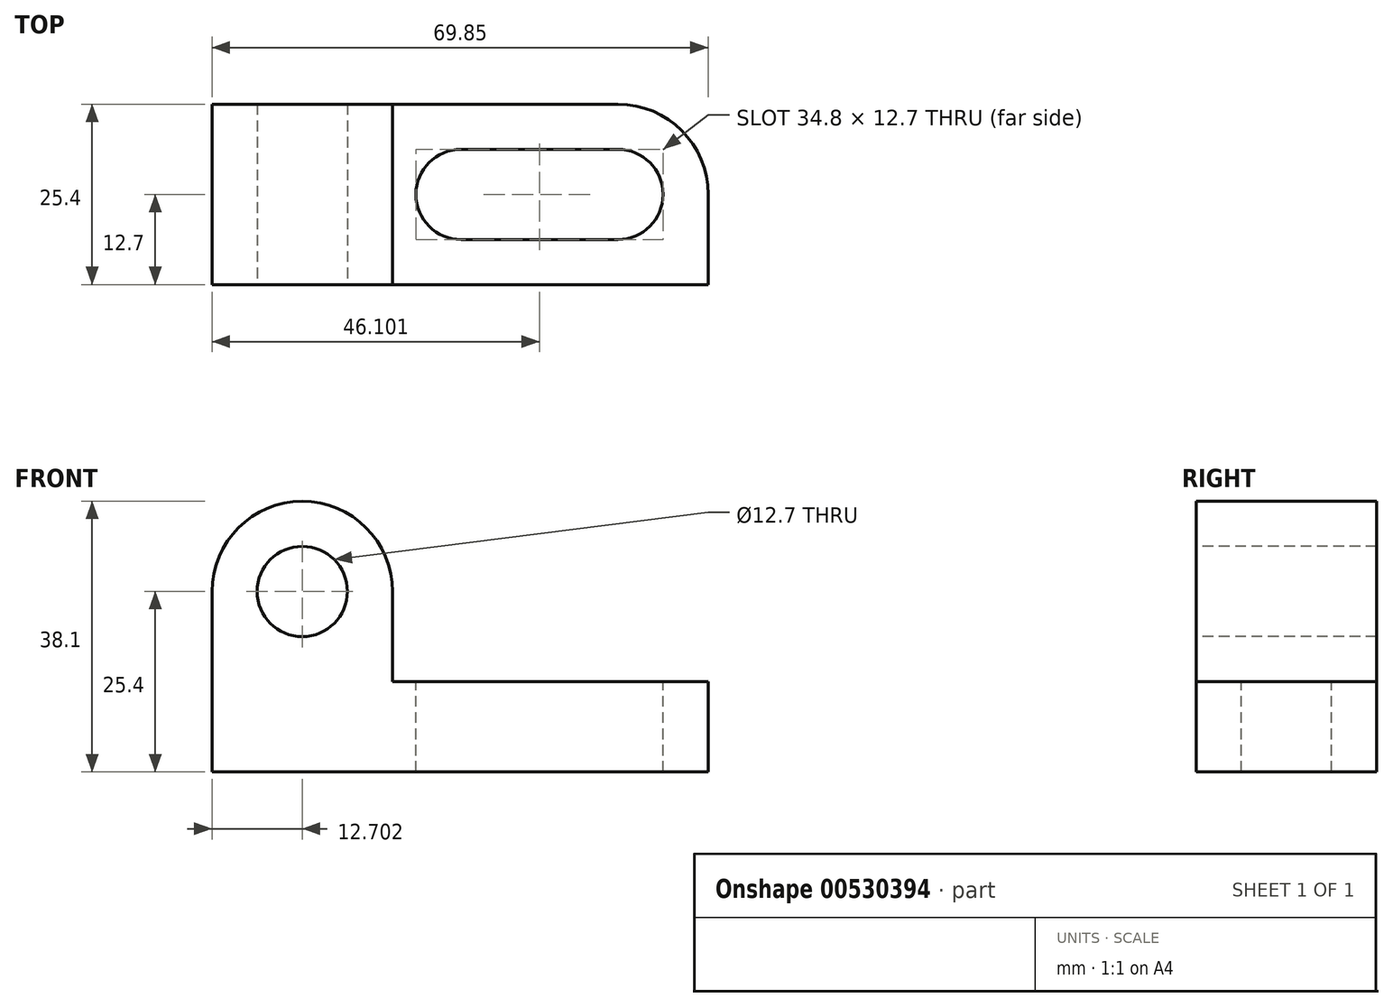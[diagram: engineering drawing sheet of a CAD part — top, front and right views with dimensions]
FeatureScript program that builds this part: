
annotation { "Feature Type Name" : "Feature", "Feature Type Description" : "" }
export const myFeature = defineFeature(function(context is Context, id is Id, definition is map)
    precondition{}
    {
        {
            var Q0;
            Q0=qCreatedBy(makeId("Front.planeOp"),FACE);
            var sketch = newSketch(context, id + "F0", { "sketchPlane" : qUnion([Q0])});
            skLineSegment(sketch, "E0", {"start": v(-35.05, 38.1) * mm, "end": v(-35.05, 0) * mm});
            skLineSegment(sketch, "E1", {"start": v(-35.05, 0) * mm, "end": v(34.8, 0) * mm});
            skLineSegment(sketch, "E2", {"start": v(34.8, 0) * mm, "end": v(34.8, 38.1) * mm});
            skLineSegment(sketch, "E3", {"start": v(34.8, 38.1) * mm, "end": v(-35.05, 38.1) * mm});
            skSolve(sketch);
        }
        {
            var Q0;
            Q0=makeQuery(id+"F0.imprint","IMPRINT",FACE,{"disambiguationData":[TD([[makeQuery(id+"F0.imprint","IMPRINT",EDGE,{"derivedFrom":sQuery(id+"F0.wireOp",EDGE,"E0")}),1.0]])]});
            extrude(context, id + "F1", {"entities" : qUnion([Q0]), "depth" : 25.4 * mm, "offsetDistance" : 25.4 * mm});
        }
        {
            var Q0;
            Q0=makeQuery(id+"F1.opExtrude","CAP_FACE",FACE,{"disambiguationData":[OSD([sQuery(id+"F0.wireOp",EDGE,"E0"),sQuery(id+"F0.wireOp",EDGE,"E1"),sQuery(id+"F0.wireOp",EDGE,"E2"),sQuery(id+"F0.wireOp",EDGE,"E3")])],"isStart":false});
            var sketch = newSketch(context, id + "F2", { "sketchPlane" : qUnion([Q0])});
            skLineSegment(sketch, "E4", {"start": v(-35.05, 38.1) * mm, "end": v(-9.65, 38.1) * mm});
            skLineSegment(sketch, "E5", {"start": v(-9.65, 38.1) * mm, "end": v(-9.65, 12.7) * mm});
            skLineSegment(sketch, "E6", {"start": v(-9.65, 12.7) * mm, "end": v(34.8, 12.7) * mm});
            skLineSegment(sketch, "E7", {"start": v(-9.65, 12.7) * mm, "end": v(-9.65, 0) * mm});
            skLineSegment(sketch, "E8", {"start": v(-35.05, 0) * mm, "end": v(-35.05, 25.4) * mm});
            skLineSegment(sketch, "E9", {"start": v(-35.05, 25.4) * mm, "end": v(-35.05, 38.1) * mm});
            skSolve(sketch);
        }
        {
            var Q0;
            {var subQ0=sQuery(id+"F2.wireOp",EDGE,"E5");Q0=makeQuery(id+"F2.imprint","IMPRINT",FACE,{"disambiguationData":[TD([[makeQuery(id+"F2.imprint","IMPRINT",EDGE,{"derivedFrom":subQ0}),1.0]])]});}
            extrude(context, id + "F3", {"entities" : qUnion([Q0]), "operationType" : NewBodyOperationType.REMOVE, "endBound" : BoundingType.THROUGH_ALL, "oppositeDirection" : true, "depth" : 25.4 * mm, "offsetDistance" : 25.4 * mm});
        }
        {
            var Q0;
            Q0=makeQuery(id+"F1.opExtrude","CAP_FACE",FACE,{"disambiguationData":[OSD([sQuery(id+"F0.wireOp",EDGE,"E0"),sQuery(id+"F0.wireOp",EDGE,"E1"),sQuery(id+"F0.wireOp",EDGE,"E2"),sQuery(id+"F0.wireOp",EDGE,"E3")])],"isStart":false});
            var sketch = newSketch(context, id + "F4", { "sketchPlane" : qUnion([Q0])});
            skLineSegment(sketch, "E10", {"start": v(-35.05, 38.1) * mm, "end": v(-35.05, 25.4) * mm});
            skLineSegment(sketch, "E11", {"start": v(-35.05, 25.4) * mm, "end": v(-35.05, 0) * mm});
            skArc(sketch, "E12", {"start": v(-9.65, 25.4) * mm, "mid": v(-22.35, 38.1) * mm, "end": v(-35.05, 25.4) * mm});
            skLineSegment(sketch, "E13", {"start": v(-35.05, 38.1) * mm, "end": v(-9.65, 38.1) * mm});
            skLineSegment(sketch, "E14", {"start": v(-9.65, 38.1) * mm, "end": v(-9.65, 25.4) * mm});
            skLineSegment(sketch, "E15", {"start": v(-9.65, 12.7) * mm, "end": v(-9.65, 0) * mm});
            skSolve(sketch);
        }
        {
            var Q0;
            {var subQ0=sQuery(id+"F4.wireOp",EDGE,"E14");Q0=makeQuery(id+"F4.imprint","IMPRINT",FACE,{"disambiguationData":[TD([[makeQuery(id+"F4.imprint","IMPRINT",EDGE,{"derivedFrom":subQ0}),-1.0]])]});}
            var Q1;
            {var subQ0=sQuery(id+"F4.wireOp",EDGE,"E10");Q1=makeQuery(id+"F4.imprint","IMPRINT",FACE,{"disambiguationData":[TD([[makeQuery(id+"F4.imprint","IMPRINT",EDGE,{"derivedFrom":subQ0}),1.0]])]});}
            extrude(context, id + "F5", {"entities" : qUnion([Q0, Q1]), "operationType" : NewBodyOperationType.REMOVE, "endBound" : BoundingType.THROUGH_ALL, "oppositeDirection" : true, "depth" : 25.4 * mm, "offsetDistance" : 25.4 * mm});
        }
        {
            var Q0;
            Q0=makeQuery(id+"F1.opExtrude","CAP_FACE",FACE,{"disambiguationData":[OSD([sQuery(id+"F0.wireOp",EDGE,"E0"),sQuery(id+"F0.wireOp",EDGE,"E1"),sQuery(id+"F0.wireOp",EDGE,"E2"),sQuery(id+"F0.wireOp",EDGE,"E3")])],"isStart":false});
            var sketch = newSketch(context, id + "F6", { "sketchPlane" : qUnion([Q0])});
            skLineSegment(sketch, "E16", {"start": v(-35.05, 25.4) * mm, "end": v(-9.65, 25.4) * mm});
            skLineSegment(sketch, "E17", {"start": v(-22.35, 38.1) * mm, "end": v(-22.35, 25.4) * mm});
            skLineSegment(sketch, "E18", {"start": v(-22.35, 25.4) * mm, "end": v(-22.35, 0) * mm});
            skCircle(sketch, "E19", {"center": v(-22.35, 25.4) * mm, "radius": 6.35 * mm});
            skLineSegment(sketch, "E20", {"start": v(-16, 25.4) * mm, "end": v(-9.65, 25.4) * mm});
            skLineSegment(sketch, "E21", {"start": v(-35.05, 25.4) * mm, "end": v(-28.7, 25.4) * mm});
            skSolve(sketch);
        }
        {
            var Q0;
            {var subQ0=sQuery(id+"F6.wireOp",EDGE,"E19");var subQ3=sQuery(id+"F6.wireOp",EDGE,"E17");var subQ5=makeQuery(id+"F6.imprint","INTERSECT",VERTEX,{"derivedFrom":[subQ3,subQ0]});Q0=makeQuery(id+"F6.imprint","IMPRINT",FACE,{"disambiguationData":[TD([[makeQuery(id+"F6.imprint","IMPRINT",EDGE,{"disambiguationData":[TD([[subQ5,-1.0]])],"derivedFrom":subQ3}),-1.0]])]});}
            var Q1;
            {var subQ0=sQuery(id+"F6.wireOp",EDGE,"E19");var subQ3=sQuery(id+"F6.wireOp",EDGE,"E17");var subQ5=makeQuery(id+"F6.imprint","INTERSECT",VERTEX,{"derivedFrom":[subQ3,subQ0]});Q1=makeQuery(id+"F6.imprint","IMPRINT",FACE,{"disambiguationData":[TD([[makeQuery(id+"F6.imprint","IMPRINT",EDGE,{"disambiguationData":[TD([[subQ5,-1.0]])],"derivedFrom":subQ3}),1.0]])]});}
            var Q2;
            {var subQ0=sQuery(id+"F6.wireOp",EDGE,"E19");var subQ3=sQuery(id+"F6.wireOp",EDGE,"E18");var subQ5=makeQuery(id+"F6.imprint","INTERSECT",VERTEX,{"derivedFrom":[subQ3,subQ0]});Q2=makeQuery(id+"F6.imprint","IMPRINT",FACE,{"disambiguationData":[TD([[makeQuery(id+"F6.imprint","IMPRINT",EDGE,{"disambiguationData":[TD([[subQ5,1.0]])],"derivedFrom":subQ3}),1.0]])]});}
            var Q3;
            {var subQ0=sQuery(id+"F6.wireOp",EDGE,"E19");var subQ3=sQuery(id+"F6.wireOp",EDGE,"E18");var subQ5=makeQuery(id+"F6.imprint","INTERSECT",VERTEX,{"derivedFrom":[subQ3,subQ0]});Q3=makeQuery(id+"F6.imprint","IMPRINT",FACE,{"disambiguationData":[TD([[makeQuery(id+"F6.imprint","IMPRINT",EDGE,{"disambiguationData":[TD([[subQ5,1.0]])],"derivedFrom":subQ3}),-1.0]])]});}
            extrude(context, id + "F7", {"entities" : qUnion([Q0, Q1, Q2, Q3]), "operationType" : NewBodyOperationType.REMOVE, "endBound" : BoundingType.THROUGH_ALL, "oppositeDirection" : true, "depth" : 25.4 * mm, "offsetDistance" : 25.4 * mm});
        }
        {
            var Q0;
            Q0=makeQuery(id+"F3.boolean.opBoolean","COPY",FACE,{"derivedFrom":makeQuery(id+"F3.opExtrude","SWEPT_FACE",FACE,{"disambiguationData":[OSD([sQuery(id+"F2.wireOp",EDGE,"E6")])]})});
            var sketch = newSketch(context, id + "F8", { "sketchPlane" : qUnion([Q0])});
            skLineSegment(sketch, "E22", {"start": v(-9.65, -25.4) * mm, "end": v(34.8, -25.4) * mm});
            skLineSegment(sketch, "E23", {"start": v(28.45, -25.4) * mm, "end": v(34.8, -25.4) * mm});
            skLineSegment(sketch, "E24", {"start": v(34.8, -25.4) * mm, "end": v(34.8, 0) * mm});
            skLineSegment(sketch, "E25", {"start": v(34.8, 0) * mm, "end": v(28.45, 0) * mm});
            skLineSegment(sketch, "E26", {"start": v(28.45, 0) * mm, "end": v(-9.65, 0) * mm});
            skLineSegment(sketch, "E27", {"start": v(28.45, 0) * mm, "end": v(22.1, 0) * mm});
            skLineSegment(sketch, "E28", {"start": v(22.1, 0) * mm, "end": v(22.1, -25.4) * mm});
            skArc(sketch, "E29", {"start": v(22.1, -25.4) * mm, "mid": v(34.8, -12.7) * mm, "end": v(22.1, 0) * mm});
            skSolve(sketch);
        }
        {
            var Q0;
            {var subQ0=sQuery(id+"F8.wireOp",EDGE,"E25");Q0=makeQuery(id+"F8.imprint","IMPRINT",FACE,{"disambiguationData":[TD([[makeQuery(id+"F8.imprint","IMPRINT",EDGE,{"derivedFrom":subQ0}),-1.0]])]});}
            var Q1;
            {var subQ0=sQuery(id+"F8.wireOp",EDGE,"E23");Q1=makeQuery(id+"F8.imprint","IMPRINT",FACE,{"disambiguationData":[TD([[makeQuery(id+"F8.imprint","IMPRINT",EDGE,{"derivedFrom":subQ0}),1.0]])]});}
            extrude(context, id + "F9", {"entities" : qUnion([Q0, Q1]), "operationType" : NewBodyOperationType.REMOVE, "endBound" : BoundingType.THROUGH_ALL, "oppositeDirection" : true, "depth" : 25.4 * mm, "offsetDistance" : 25.4 * mm});
        }
        {
            var Q0;
            Q0=makeQuery(id+"F3.boolean.opBoolean","COPY",FACE,{"derivedFrom":makeQuery(id+"F3.opExtrude","SWEPT_FACE",FACE,{"disambiguationData":[OSD([sQuery(id+"F2.wireOp",EDGE,"E6")])]})});
            var sketch = newSketch(context, id + "F10", { "sketchPlane" : qUnion([Q0])});
            skLineSegment(sketch, "E30", {"start": v(0, -6.35) * mm, "end": v(0, -19.05) * mm});
            skLineSegment(sketch, "E31", {"start": v(0, -19.05) * mm, "end": v(22.1, -19.05) * mm});
            skLineSegment(sketch, "E32", {"start": v(22.1, -19.05) * mm, "end": v(22.1, -6.35) * mm});
            skLineSegment(sketch, "E33", {"start": v(22.1, -6.35) * mm, "end": v(0, -6.35) * mm});
            skSolve(sketch);
        }
        {
            var Q0;
            Q0 = qSketchRegion(id + "F10", true);
            var Q1;
            Q1=makeQuery(id+"F10.imprint","IMPRINT",FACE,{"disambiguationData":[TD([[makeQuery(id+"F10.imprint","IMPRINT",EDGE,{"derivedFrom":sQuery(id+"F10.wireOp",EDGE,"E30")}),1.0]])]});
            extrude(context, id + "F11", {"entities" : qUnion([Q0, Q1]), "operationType" : NewBodyOperationType.REMOVE, "oppositeDirection" : true, "depth" : 25.4 * mm, "offsetDistance" : 25.4 * mm});
        }
        {
            var Q0;
            Q0=makeQuery(id+"F3.boolean.opBoolean","COPY",FACE,{"derivedFrom":makeQuery(id+"F3.opExtrude","SWEPT_FACE",FACE,{"disambiguationData":[OSD([sQuery(id+"F2.wireOp",EDGE,"E6")])]})});
            var sketch = newSketch(context, id + "F12", { "sketchPlane" : qUnion([Q0])});
            skArc(sketch, "E34", {"start": v(22.1, -19.05) * mm, "mid": v(28.45, -12.7) * mm, "end": v(22.1, -6.35) * mm});
            skArc(sketch, "E35", {"start": v(0, -6.35) * mm, "mid": v(-6.35, -12.7) * mm, "end": v(0, -19.05) * mm});
            skSolve(sketch);
        }
        {
            var Q0;
            Q0=makeQuery(id+"F12.imprint","IMPRINT",FACE,{"disambiguationData":[TD([[makeQuery(id+"F12.imprint","IMPRINT",EDGE,{"derivedFrom":sQuery(id+"F12.wireOp",EDGE,"E35")}),1.0]])]});
            var Q1;
            Q1=makeQuery(id+"F12.imprint","IMPRINT",FACE,{"disambiguationData":[TD([[makeQuery(id+"F12.imprint","IMPRINT",EDGE,{"derivedFrom":sQuery(id+"F12.wireOp",EDGE,"E34")}),1.0]])]});
            extrude(context, id + "F13", {"entities" : qUnion([Q0, Q1]), "operationType" : NewBodyOperationType.REMOVE, "endBound" : BoundingType.THROUGH_ALL, "oppositeDirection" : true, "depth" : 25.4 * mm, "offsetDistance" : 25.4 * mm});
        }
    });
